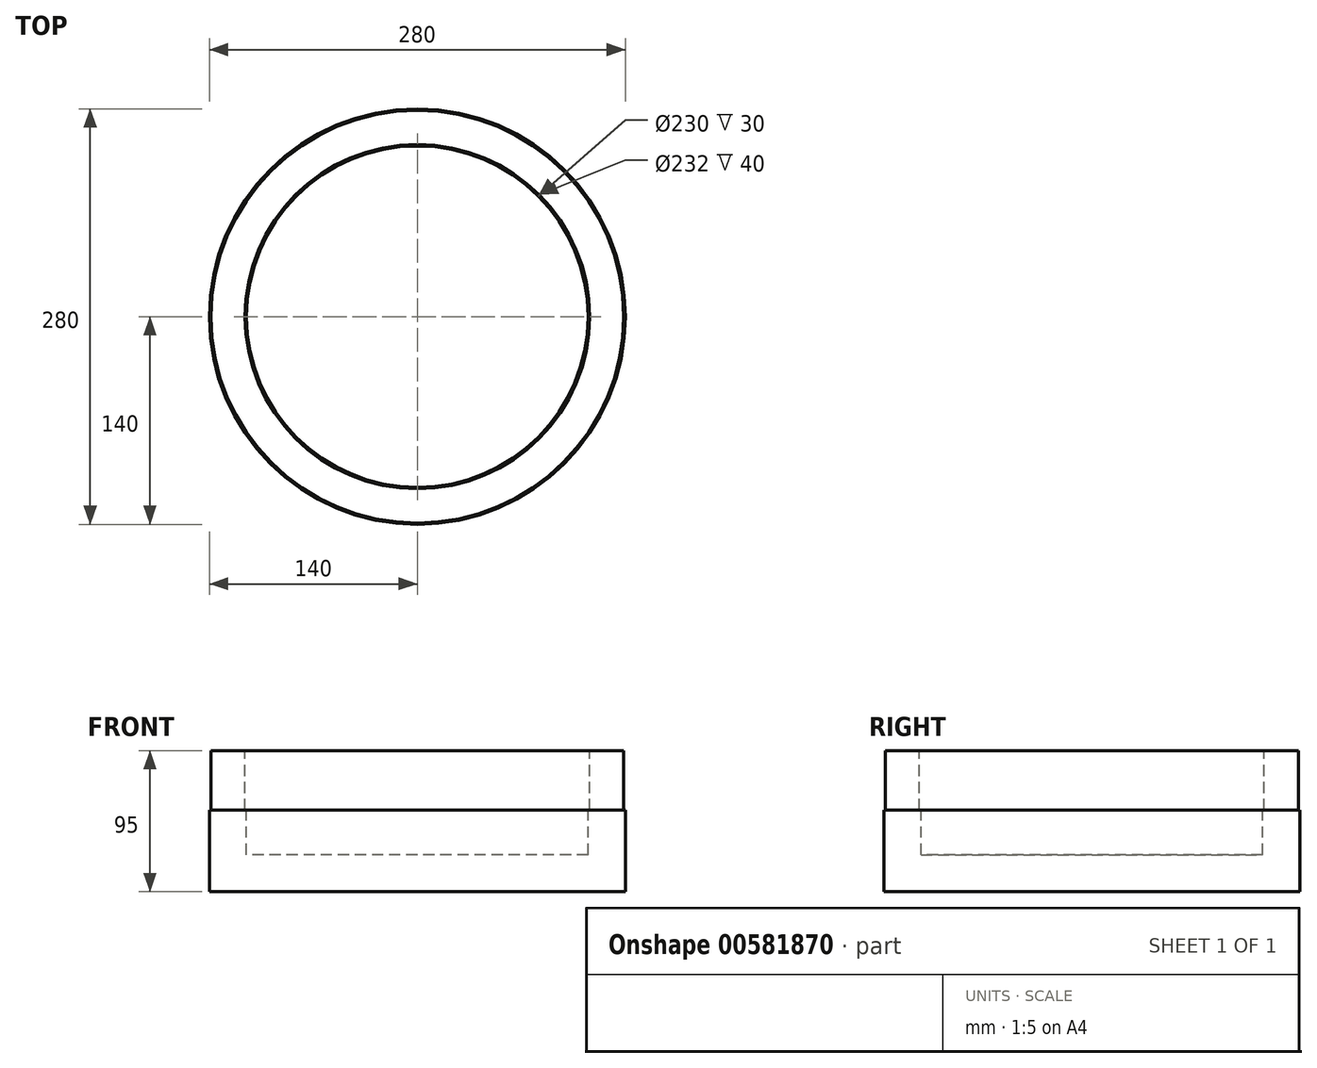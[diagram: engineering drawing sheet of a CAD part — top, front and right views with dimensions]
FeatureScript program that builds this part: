
annotation { "Feature Type Name" : "Feature", "Feature Type Description" : "" }
export const myFeature = defineFeature(function(context is Context, id is Id, definition is map)
    precondition{}
    {
        {
            var Q0;
            Q0=qCreatedBy(makeId("Front.planeOp"),FACE);
            var sketch = newSketch(context, id + "F0", { "sketchPlane" : qUnion([Q0])});
            skLineSegment(sketch, "E0", {"start": v(0, 136.7) * mm, "end": v(0, 0) * mm, "construction": true});
            skLineSegment(sketch, "E1", {"start": v(0, 0) * mm, "end": v(-140, 0) * mm});
            skLineSegment(sketch, "E2", {"start": v(-140, 0) * mm, "end": v(-140, 55) * mm});
            skLineSegment(sketch, "E3", {"start": v(-140, 55) * mm, "end": v(-139, 55) * mm});
            skLineSegment(sketch, "E4", {"start": v(-139, 55) * mm, "end": v(-139, 95) * mm});
            skLineSegment(sketch, "E5", {"start": v(-139, 95) * mm, "end": v(-116, 95) * mm});
            skLineSegment(sketch, "E6", {"start": v(-116, 95) * mm, "end": v(-116, 55) * mm});
            skLineSegment(sketch, "E7", {"start": v(-116, 55) * mm, "end": v(-115, 55) * mm});
            skLineSegment(sketch, "E8", {"start": v(-115, 55) * mm, "end": v(-115, 25) * mm});
            skLineSegment(sketch, "E9", {"start": v(-115, 25) * mm, "end": v(0, 25) * mm});
            skLineSegment(sketch, "E10", {"start": v(0, 25) * mm, "end": v(0, 0) * mm});
            skSolve(sketch);
        }
        {
            var Q0;
            Q0=qSketchRegion(id+"F0",true);
            var Q1;
            Q1=sQuery(id+"F0.wireOp",EDGE,"E0");
            revolve(context, id + "F1", {"surfaceOperationType" : NewSurfaceOperationType.NEW, "entities" : qUnion([Q0]), "axis" : qUnion([Q1]), "revolveType" : RevolveType.FULL});
        }
    });
